# Revit family: QF_BOURGEAT_Satellite4G_GN6_pied_inox_froid
name_source: partatom
category: Equipement spécialisé
revit_build: Autodesk Revit 2015 (Build: 20140606_1530(x64)
units: mm (PartAtom-declared; Revit-internal decimal feet)

## types (2) — shared parameters
Certification = NF hygiene alimentaire
Charge max = 60.00 kg
Charge_gaz = 0.150 Kg
Classe Climatique = 4
Consommation énergétique = 2.4Kwh/h NFD40-016
Diametre_roue = 80 mm  [stored 0.262467 ft]
Fabricant = BOURGEAT
Fréquence = 50 Hz
Hauteur hors tout = 727 mm  [stored 2.38517 ft]
Hauteur_pied_inox = 154 mm
Hauteur_poignee_porte_sol = 241 mm  [stored 0.790682 ft]
Hauteur_poignees_laterales = 804 mm  [stored 2.6378 ft]
Hauteur_porte = 534 mm
Indice de protection = IP25
Intensité nominale = 1 A
Largeur_porte = 706 mm  [stored 2.31627 ft]
Longueur hors tout = 752 mm  [stored 2.46719 ft]
Longueur_poignees_laterales = 609 mm  [stored 1.99803 ft]
Materiau_Poignee_porte = B_Elastomère_TPE_S
Materiau_bac = Acier inoxydable, brossé
Materiau_bandage = B_Elastomère_TPE_S
Materiau_porte = Acier inoxydable, brossé
Materiau_vitre = Verre, vitrage transparent, trempé
Nature isolant = Mousse sans PU
Phase = 2
Poids net à vide = 65.00 kg
Pos_V_IHM = 38 mm  [stored 0.124672 ft]
Profondeur hors tout = 765 mm  [stored 2.50984 ft]
Puissance électrique  = 300 W
Spécification du Fabricant = Satellite 4G
Tension = 230 V
Type Fluide Frigorigène = R134a
URL catalogue = http://www.bourgeat.fr

## per-type parameters (varying)
| type | Modèle | Poignee_droite | Poignee_gauche | Puissance frigorifique |
| GN6_1/1_entree530_porte_inox_tirant_gauche | 842006 + 844017 | Non | Oui | 270 W à-5°C |
| GN6_1/1_entree530_porte_inox_tirant_droit | 842006 + 844000 + 844017 | Oui | Non | 270 W à -5°C |

note: [stored X ft] marks values corroborated as IEEE doubles in the binary element streams (Revit-internal decimal feet)
